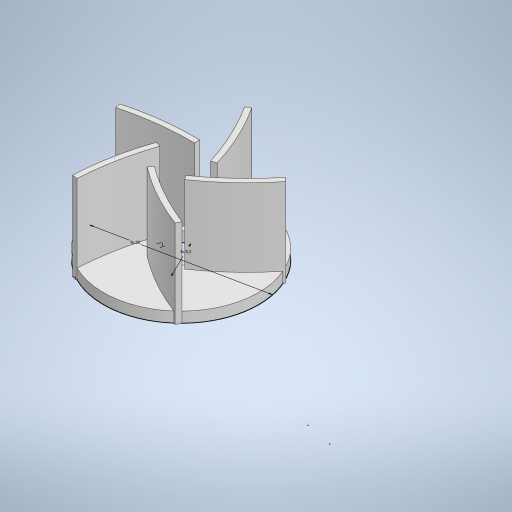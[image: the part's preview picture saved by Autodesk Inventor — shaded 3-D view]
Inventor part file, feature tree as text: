
AUTODESK INVENTOR PART (.ipt)
format: ipt  version: 2023.1 (Build 271208000, 208)  size: 283,136 bytes
history: native  units: in
note: dims shown in document units (in); Inventor stores cm internally (conversion verified against a paired STEP export)
features: extrude x2, other x1, sketch x1, pattern_circular x1
ambient origin geometry x8: Origin, YZ Plane, XZ Plane, XY Plane, X Axis, Y Axis, Z Axis, Center Point
bodies: Solid1 (feature_tree)
feature tree (5):
  other  "<userpath>\Documents\WaterPump\Parameters.xlsx"
  sketch  "Sketch1"  dims[d0=1.1811in d1=0.3228in d2=0.0787in d3=0.0in d10=0.0394in d11=0.0394in d12=0.6693in d13=0.0in d14=1.9685in d15=360.0deg]
  extrude  "Extrusion1"  Depth=0.6693in
  extrude  "Extrusion3"  Depth=0.0787in TaperAngle=0.0deg
  pattern_circular  "Circular Pattern2"  [2 undecoded]
note: 2 required parameter values undecoded (feature->parameter linkage not recoverable at this tier; creation-order binding heuristic only, values carry confidence <= 0.55)
